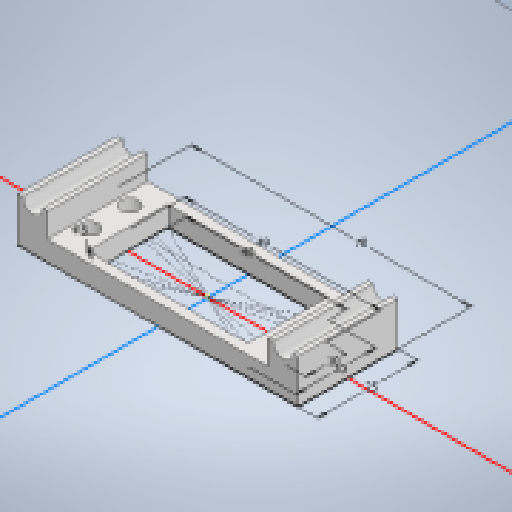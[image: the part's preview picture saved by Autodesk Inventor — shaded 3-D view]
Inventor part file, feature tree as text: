
AUTODESK INVENTOR PART (.ipt)
format: ipt  version: 2025.2 (Build 292293000, 293)  size: 186,368 bytes
history: native  units: mm
features: extrude x3, sketch x2, mirror x1
ambient origin geometry x8: Origin, YZ Plane, XZ Plane, XY Plane, X Axis, Y Axis, Z Axis, Center Point
bodies: Solid1 (feature_tree)
feature tree (6):
  sketch  "Sketch1"  dims[d0=10.0mm d1=49.0mm]
  extrude  "Extrusion1"  Depth=10.0mm
  sketch  "Sketch2"  dims[d2=4.5mm d3=5.0mm d4=0.0mm d5=25.0mm d6=70.0mm d7=20.0mm d8=40.0mm d9=5.0mm d10=7.5mm d12=6.0mm d13=5.0mm d14=0.0mm d18=0.2mm d19=2.0mm d20=0.0mm]
  extrude  "Extrusion2"  Depth=5.0mm TaperAngle=0.0deg
  extrude  "Extrusion4"  Depth=25.0mm
  mirror  "Mirror1"
